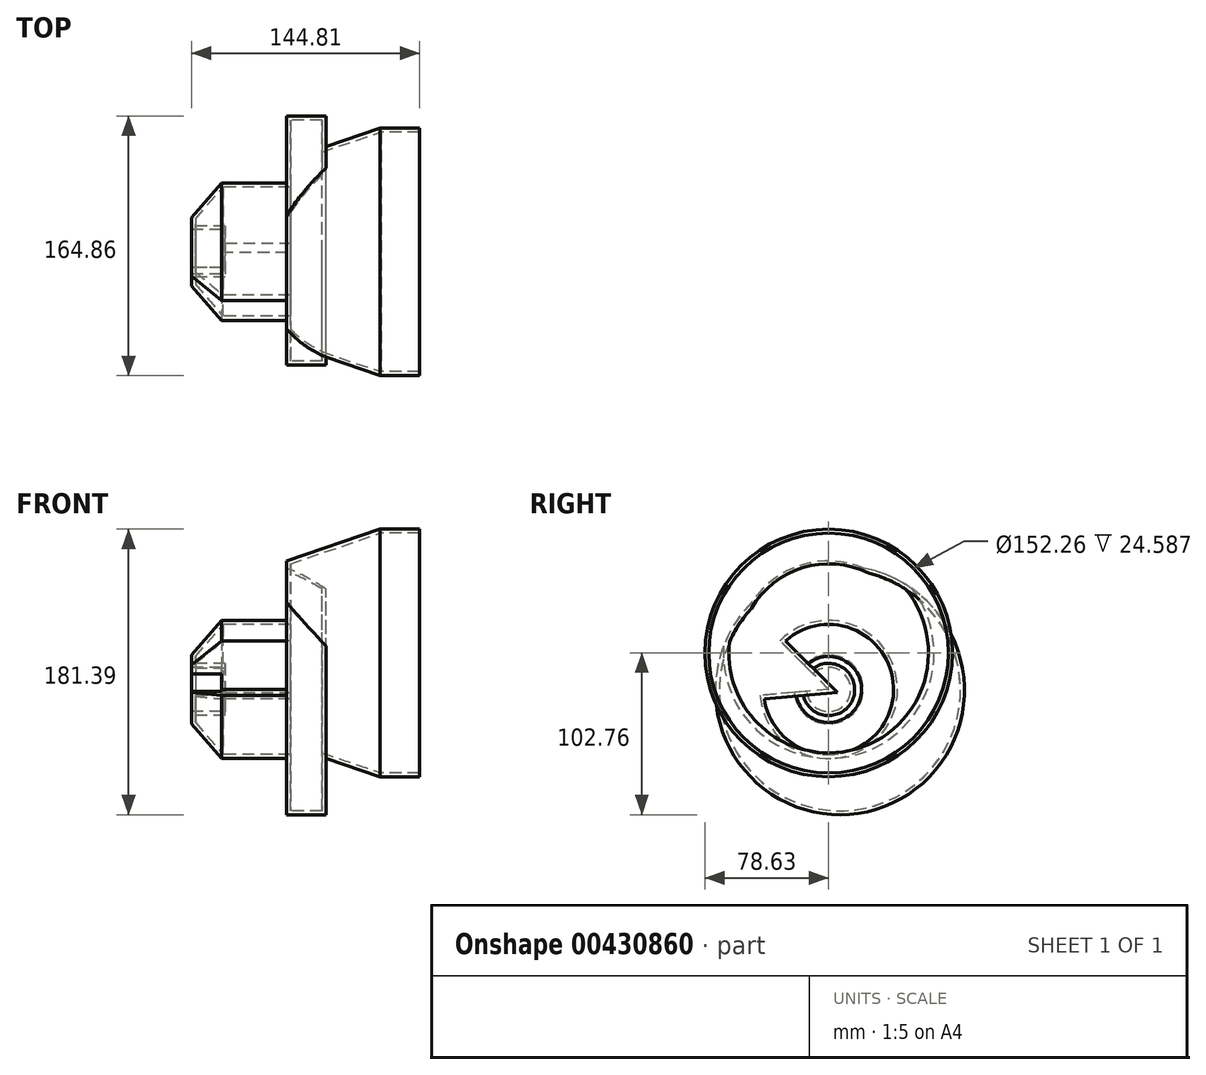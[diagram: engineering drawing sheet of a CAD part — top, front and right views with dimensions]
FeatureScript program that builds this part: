
annotation { "Feature Type Name" : "Feature", "Feature Type Description" : "" }
export const myFeature = defineFeature(function(context is Context, id is Id, definition is map)
    precondition{}
    {
        {
            var Q0;
            Q0=qCreatedBy(makeId("Front.planeOp"),FACE);
            var sketch = newSketch(context, id + "F0", { "sketchPlane" : qUnion([Q0])});
            skLineSegment(sketch, "E0", {"start": v(0, 23.17) * mm, "end": v(66.87, 23.17) * mm, "construction": true});
            skLineSegment(sketch, "E1", {"start": v(0, 81.59) * mm, "end": v(59.48, 101.8) * mm});
            skLineSegment(sketch, "E2", {"start": v(59.48, 101.8) * mm, "end": v(59.48, 45.35) * mm});
            skLineSegment(sketch, "E3", {"start": v(59.48, 45.35) * mm, "end": v(59.48, 23.17) * mm});
            skLineSegment(sketch, "E4", {"start": v(59.48, 23.17) * mm, "end": v(0, 23.17) * mm});
            skLineSegment(sketch, "E5", {"start": v(0, 98.1) * mm, "end": v(0, 23.17) * mm});
            skSolve(sketch);
        }
        {
            var Q0;
            {var subQ1=sQuery(id+"F0.wireOp",EDGE,"E1");Q0=makeQuery(id+"F0.imprint","IMPRINT",FACE,{"disambiguationData":[TD([[makeQuery(id+"F0.imprint","IMPRINT",EDGE,{"derivedFrom":subQ1}),-1.0]])]});}
            var Q1;
            Q1=sQuery(id+"F0.wireOp",EDGE,"E0");
            revolve(context, id + "F1", {"entities" : qUnion([Q0]), "axis" : qUnion([Q1]), "revolveType" : RevolveType.FULL});
        }
        {
            var Q0;
            Q0=qCreatedBy(makeId("Front.planeOp"),FACE);
            var sketch = newSketch(context, id + "F2", { "sketchPlane" : qUnion([Q0])});
            skLineSegment(sketch, "E6.bottom", {"start": v(-41.4, 0) * mm, "end": v(0, 0) * mm});
            skLineSegment(sketch, "E6.top", {"start": v(-41.4, 43.79) * mm, "end": v(0, 43.79) * mm});
            skLineSegment(sketch, "E6.left", {"start": v(-41.4, 0) * mm, "end": v(-41.4, 14.06) * mm});
            skLineSegment(sketch, "E6.right", {"start": v(0, 0) * mm, "end": v(0, 43.79) * mm});
            skLineSegment(sketch, "E7", {"start": v(-60.33, 21.9) * mm, "end": v(-41.4, 43.79) * mm});
            skLineSegment(sketch, "E8", {"start": v(-41.4, 14.06) * mm, "end": v(-60.33, 14.06) * mm});
            skLineSegment(sketch, "E9", {"start": v(-60.33, 14.06) * mm, "end": v(-60.33, 21.9) * mm});
            skPoint(sketch, "E10.orphan", {"position": v(0, 21.9) * mm});
            skSolve(sketch);
        }
        {
            var Q0;
            Q0=makeQuery(id+"F2.imprint","IMPRINT",FACE,{"disambiguationData":[TD([[makeQuery(id+"F2.imprint","IMPRINT",EDGE,{"derivedFrom":sQuery(id+"F2.wireOp",EDGE,"E6.bottom")}),1.0]])]});
            var Q1;
            Q1=sQuery(id+"F2.wireOp",EDGE,"E6.bottom");
            revolve(context, id + "F3", {"entities" : qUnion([Q0]), "axis" : qUnion([Q1]), "revolveType" : RevolveType.TWO_DIRECTIONS, "angle" : 45 * degree, "angleBack" : 95 * degree});
        }
        {
            var Q0;
            Q0=qCreatedBy(makeId("Right.planeOp"),FACE);
            var sketch = newSketch(context, id + "F4", { "sketchPlane" : qUnion([Q0])});
            skLineSegment(sketch, "E11", {"start": v(105.5, 47.88) * mm, "end": v(-112.93, 47.88) * mm, "construction": true});
            skPoint(sketch, "E12.end.orphan", {"position": v(-112.93, 0) * mm});
            skLineSegment(sketch, "E13", {"start": v(104.66, 0) * mm, "end": v(-112.93, 0) * mm});
            skCircle(sketch, "E14", {"center": v(7.17, -0.52) * mm, "radius": 79.07 * mm});
            skPoint(sketch, "E14.first.point", {"position": v(79.3, 31.85) * mm});
            skPoint(sketch, "E14.second.point", {"position": v(-55.44, -48.81) * mm});
            skPoint(sketch, "E14.third.point", {"position": v(69.69, 47.88) * mm});
            skSolve(sketch);
        }
        {
            var Q0;
            Q0=makeQuery(id+"F1.opRevolve","SWEPT_FACE",FACE,{"disambiguationData":[OSD([sQuery(id+"F0.wireOp",EDGE,"E2"),sQuery(id+"F0.wireOp",EDGE,"E3")])]});
            extrude(context, id + "F5", {"entities" : qUnion([Q0]), "operationType" : NewBodyOperationType.ADD, "depth" : 25 * mm});
        }
        {
            var Q0;
            {var subQ0=sQuery(id+"F4.wireOp",EDGE,"E14");var subQ1=sQuery(id+"F4.wireOp",EDGE,"E13");var subQ2=makeQuery(id+"F4.imprint","INTERSECT",VERTEX,{"disambiguationData":[OD(0.0)],"derivedFrom":[subQ1,subQ0]});Q0=makeQuery(id+"F4.imprint","IMPRINT",FACE,{"disambiguationData":[TD([[makeQuery(id+"F4.imprint","IMPRINT",EDGE,{"disambiguationData":[TD([[subQ2,1.0]])],"derivedFrom":subQ1}),1.0]])]});}
            var Q1;
            {var subQ0=sQuery(id+"F4.wireOp",EDGE,"E14");var subQ1=sQuery(id+"F4.wireOp",EDGE,"E13");var subQ2=makeQuery(id+"F4.imprint","INTERSECT",VERTEX,{"disambiguationData":[OD(0.0)],"derivedFrom":[subQ1,subQ0]});Q1=makeQuery(id+"F4.imprint","IMPRINT",FACE,{"disambiguationData":[TD([[makeQuery(id+"F4.imprint","IMPRINT",EDGE,{"disambiguationData":[TD([[subQ2,1.0]])],"derivedFrom":subQ1}),-1.0]])]});}
            extrude(context, id + "F6", {"entities" : qUnion([Q0, Q1]), "operationType" : NewBodyOperationType.ADD, "depth" : 25 * mm});
        }
        {
            var Q0;
            Q0=qCreatedBy(makeId("Front.planeOp"),FACE);
            var sketch = newSketch(context, id + "F7", { "sketchPlane" : qUnion([Q0])});
            skCircle(sketch, "E15", {"center": v(22.08, 46.03) * mm, "radius": 10.3 * mm});
            skSolve(sketch);
        }
        {
            var Q0;
            Q0=sQuery(id+"F7.wireOp",EDGE,"E15");
            extrude(context, id + "F8", {"bodyType" : ToolBodyType.SURFACE, "surfaceEntities" : qUnion([Q0]), "endBound" : BoundingType.SYMMETRIC, "oppositeDirection" : true, "depth" : 233.97 * mm, "hasSecondDirection" : true, "secondDirectionBound" : SecondDirectionBoundingType.THROUGH_ALL, "secondDirectionOppositeDirection" : false, "secondDirectionDepth" : 94.1 * mm});
        }
        {
            var Q0;
            Q0=makeQuery(id+"F5.opExtrude","CAP_FACE",FACE,{"disambiguationData":[OSD([sQuery(id+"F0.wireOp",EDGE,"E2"),sQuery(id+"F0.wireOp",EDGE,"E3")])],"isStart":false});
            shell(context, id + "F9", {"entities" : qUnion([Q0]), "thickness" : 2.5 * mm});
        }
    });
